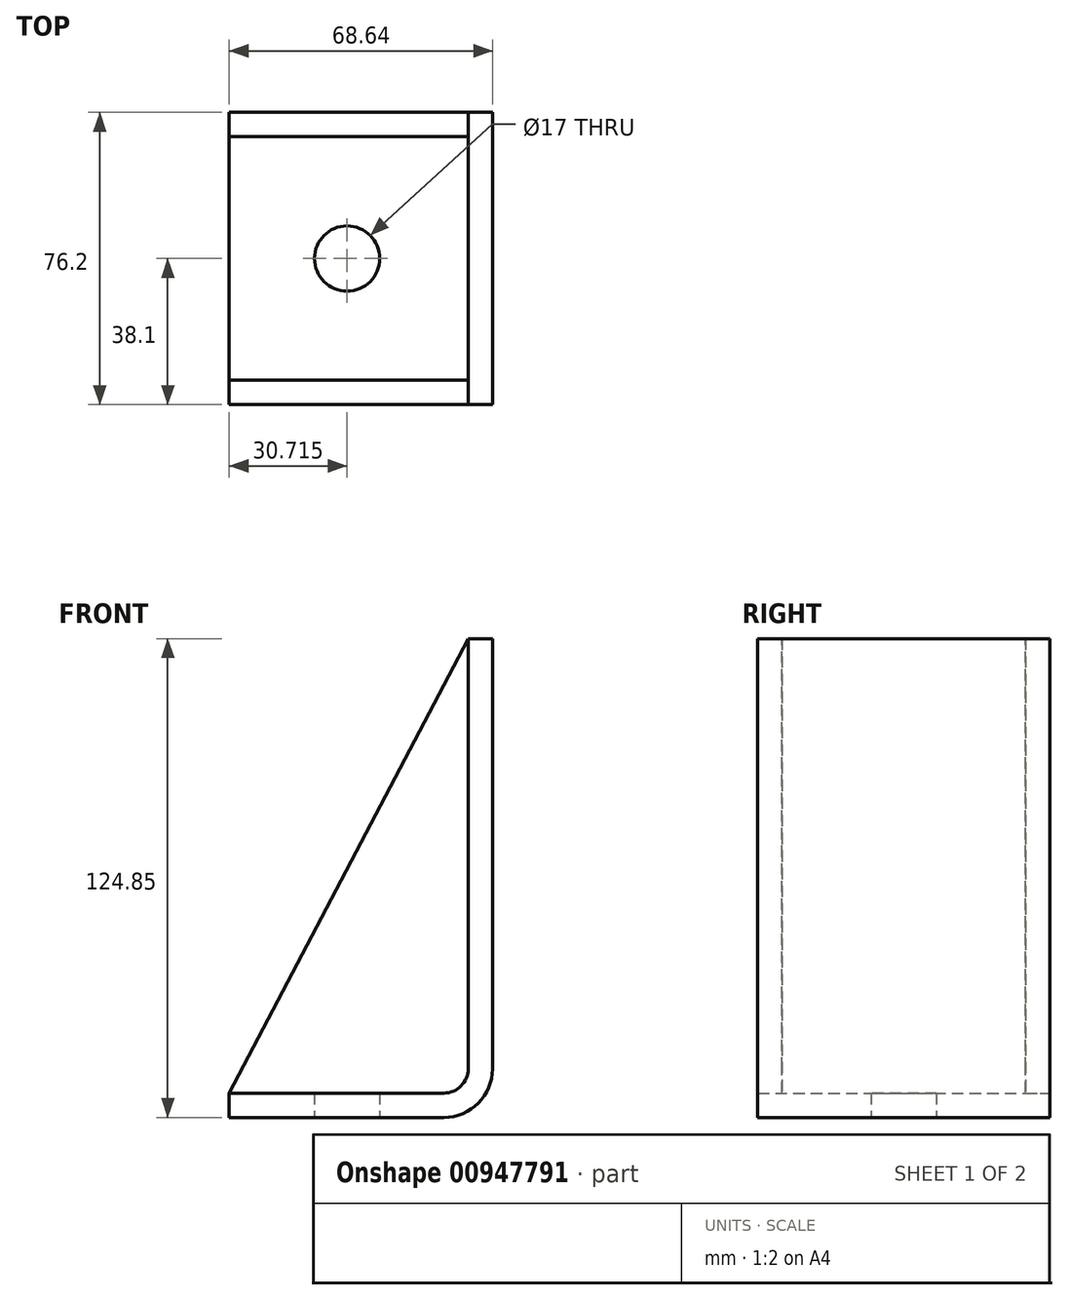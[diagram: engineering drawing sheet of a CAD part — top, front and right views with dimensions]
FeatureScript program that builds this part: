
annotation { "Feature Type Name" : "Feature", "Feature Type Description" : "" }
export const myFeature = defineFeature(function(context is Context, id is Id, definition is map)
    precondition{}
    {
        {
            var Q0;
            Q0=qCreatedBy(makeId("Front.planeOp"),FACE);
            var sketch = newSketch(context, id + "F0", { "sketchPlane" : qUnion([Q0])});
            skLineSegment(sketch, "E0", {"start": v(-62.28, -118.5) * mm, "end": v(-6.35, -118.5) * mm});
            skLineSegment(sketch, "E1", {"start": v(0, -112.15) * mm, "end": v(0, 0) * mm});
            skLineSegment(sketch, "E2", {"start": v(0, 0) * mm, "end": v(-62.29, -118.5) * mm});
            skArc(sketch, "E3.filletArc", {"start": v(-6.35, -118.5) * mm, "mid": v(-1.86, -116.64) * mm, "end": v(0, -112.15) * mm});
            skLineSegment(sketch, "E4.top", {"start": v(-62.29, -118.5) * mm, "end": v(-62.29, -118.5) * mm});
            skPoint(sketch, "E5.visualSharp", {"position": v(0, -118.5) * mm});
            skSolve(sketch);
        }
        {
            var Q0;
            Q0 = qSketchRegion(id + "F0", true);
            extrude(context, id + "F1", {"entities" : qUnion([Q0]), "depth" : 6.35 * mm, "offsetDistance" : 25 * mm});
        }
        {
            var Q0;
            Q0=qCreatedBy(makeId("Front.planeOp"),FACE);
            var sketch = newSketch(context, id + "F2", { "sketchPlane" : qUnion([Q0])});
            skLineSegment(sketch, "E6", {"start": v(0, 0) * mm, "end": v(6.35, 0) * mm});
            skLineSegment(sketch, "E7", {"start": v(6.35, 0) * mm, "end": v(6.35, -112.15) * mm});
            skLineSegment(sketch, "E8", {"start": v(-62.28, -118.5) * mm, "end": v(-62.28, -124.85) * mm});
            skLineSegment(sketch, "E9", {"start": v(-62.28, -124.85) * mm, "end": v(-6.35, -124.85) * mm});
            skLineSegment(sketch, "E10", {"start": v(-62.28, -118.5) * mm, "end": v(-6.35, -118.5) * mm});
            skLineSegment(sketch, "E11", {"start": v(0, -112.15) * mm, "end": v(0, 0) * mm});
            skPoint(sketch, "E12.visualSharp", {"position": v(0, -118.5) * mm});
            skArc(sketch, "E12.filletArc", {"start": v(-6.35, -118.5) * mm, "mid": v(-1.86, -116.64) * mm, "end": v(0, -112.15) * mm});
            skArc(sketch, "E13.filletArc", {"start": v(-6.35, -124.85) * mm, "mid": v(2.63, -121.13) * mm, "end": v(6.35, -112.15) * mm});
            skSolve(sketch);
        }
        {
            var Q0;
            Q0 = qSketchRegion(id + "F2", true);
            extrude(context, id + "F3", {"entities" : qUnion([Q0]), "depth" : 76.2 * mm, "offsetDistance" : 25 * mm});
        }
        {
            var Q0;
            Q0=makeQuery(id+"F1.opExtrude","SWEPT_BODY",BODY,{"disambiguationData":[OSD([sQuery(id+"F0.wireOp",EDGE,"E0"),sQuery(id+"F0.wireOp",EDGE,"E1"),sQuery(id+"F0.wireOp",EDGE,"E2"),sQuery(id+"F0.wireOp",EDGE,"E3.filletArc")])]});
            transform(context, id + "F4", {"entities" : qUnion([Q0]), "transformType" : TransformType.TRANSLATION_3D, "dx" : 0 * mm, "dy" : -69.85 * mm, "dz" : 0 * mm, "makeCopy" : true});
        }
        {
            var Q0;
            Q0=makeQuery(id+"F3.opExtrude","SWEPT_FACE",FACE,{"disambiguationData":[OSD([sQuery(id+"F2.wireOp",EDGE,"E10")])]});
            var sketch = newSketch(context, id + "F5", { "sketchPlane" : qUnion([Q0])});
            skPoint(sketch, "E14", {"position": v(-31.57, -38.1) * mm});
            skPoint(sketch, "E14.positionSnap0", {"position": v(-62.28, -38.1) * mm});
            skSolve(sketch);
        }
        {
            var Q0;
            Q0=sQuery(id+"F5.wireOp",VERTEX,"E14");
            var Q1;
            Q1=makeQuery(id+"F3.opExtrude","SWEPT_BODY",BODY,{"disambiguationData":[OSD([sQuery(id+"F2.wireOp",EDGE,"E6"),sQuery(id+"F2.wireOp",EDGE,"E7"),sQuery(id+"F2.wireOp",EDGE,"E8"),sQuery(id+"F2.wireOp",EDGE,"E9"),sQuery(id+"F2.wireOp",EDGE,"E10"),sQuery(id+"F2.wireOp",EDGE,"E11"),sQuery(id+"F2.wireOp",EDGE,"E12.filletArc"),sQuery(id+"F2.wireOp",EDGE,"E13.filletArc")])]});
            hole(context, id + "F6", {"style" : HoleStyle.SIMPLE, "endStyle" : HoleEndStyle.BLIND, "standardTappedOrClearance" : lookupTablePath({ "fit" : "Close", "standard" : "ISO", "size" : "M16", "type" : "Clearance" }), "standardBlindInLast" : lookupTablePath({ "fit" : "Close", "standard" : "ISO", "engagement" : "75%", "pitch" : "2 mm", "size" : "M16", "type" : "Clearance & tapped" }), "holeDiameter" : 17 * mm, "majorDiameter" : 5 * mm, "holeDepth" : 6.35 * mm, "isTappedThrough" : true, "tappedDepth" : 40.45 * mm, "tapClearance" : 3, "locations" : qUnion([Q0]), "scope" : qUnion([Q1]), "startStyle" : HoleStartStyle.SKETCH});
        }
    });
